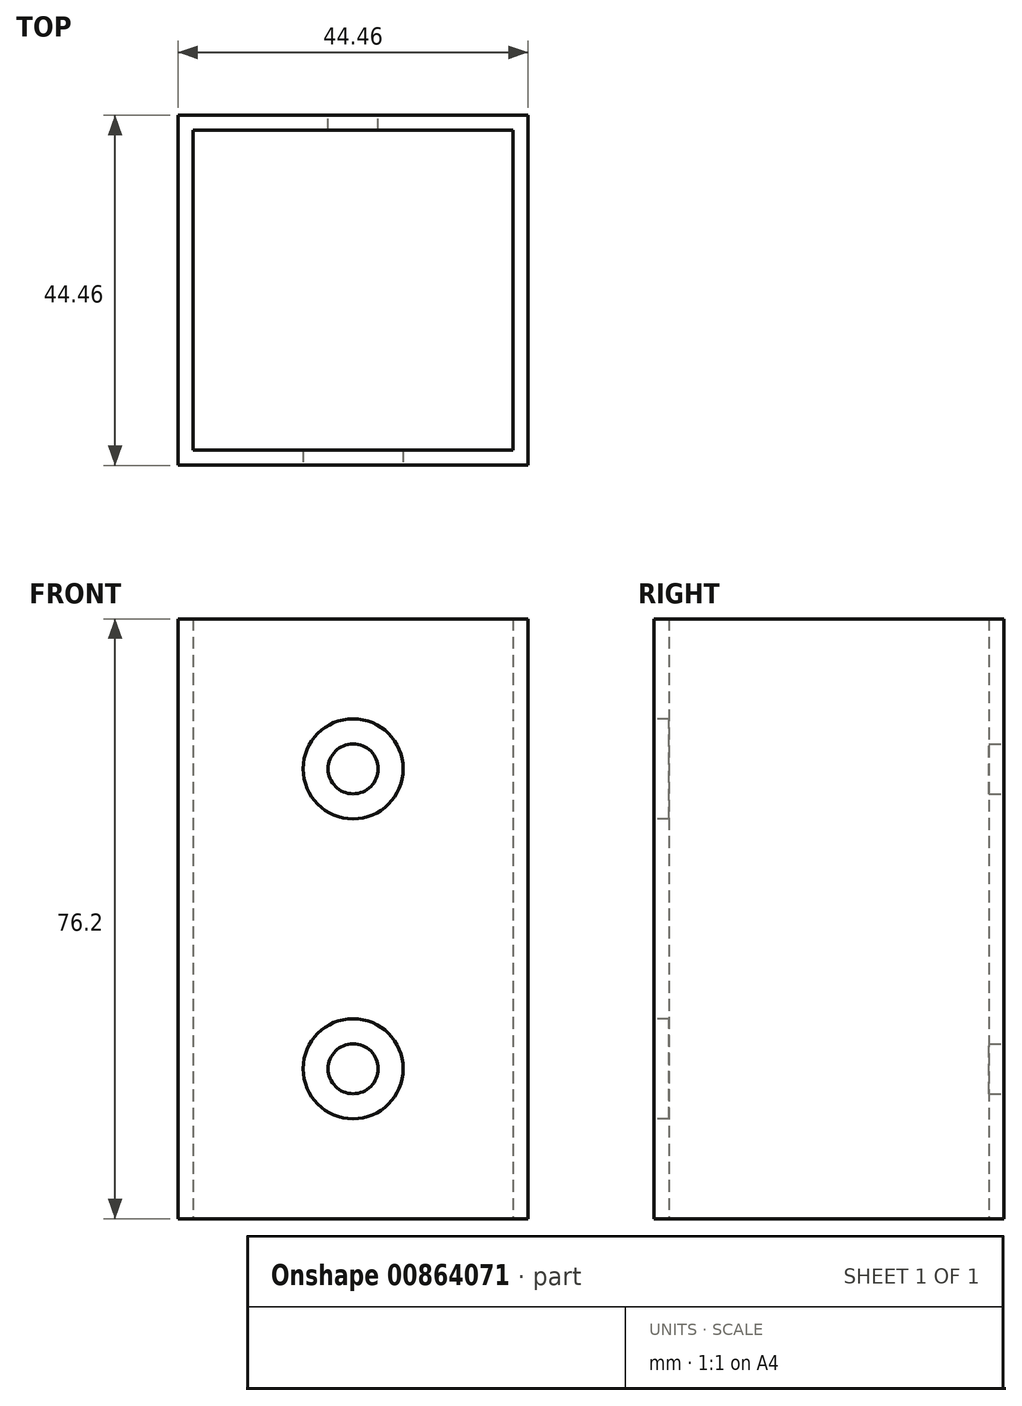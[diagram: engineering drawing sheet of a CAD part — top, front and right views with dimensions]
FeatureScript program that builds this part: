
annotation { "Feature Type Name" : "Feature", "Feature Type Description" : "" }
export const myFeature = defineFeature(function(context is Context, id is Id, definition is map)
    precondition{}
    {
        {
            var Q0;
            Q0=qCreatedBy(makeId("Top.planeOp"),FACE);
            var sketch = newSketch(context, id + "F0", { "sketchPlane" : qUnion([Q0])});
            skLineSegment(sketch, "E0.bottom", {"start": v(20.32, 20.32) * mm, "end": v(-20.32, 20.32) * mm});
            skLineSegment(sketch, "E0.top", {"start": v(20.32, -20.32) * mm, "end": v(-20.32, -20.32) * mm});
            skLineSegment(sketch, "E0.left", {"start": v(20.32, 20.32) * mm, "end": v(20.32, -20.32) * mm});
            skLineSegment(sketch, "E0.right", {"start": v(-20.32, 20.32) * mm, "end": v(-20.32, -20.32) * mm});
            skPoint(sketch, "E0.middle", {"position": v(0, 0) * mm});
            skLineSegment(sketch, "E1.bottom", {"start": v(22.23, 22.23) * mm, "end": v(-22.23, 22.22) * mm});
            skLineSegment(sketch, "E1.top", {"start": v(22.23, -22.22) * mm, "end": v(-22.23, -22.23) * mm});
            skLineSegment(sketch, "E1.left", {"start": v(22.23, 22.23) * mm, "end": v(22.23, -22.22) * mm});
            skLineSegment(sketch, "E1.right", {"start": v(-22.23, 22.22) * mm, "end": v(-22.23, -22.23) * mm});
            skSolve(sketch);
        }
        {
            var Q0;
            Q0 = qSketchRegion(id + "F0", true);
            extrude(context, id + "F1", {"entities" : qUnion([Q0]), "depth" : 76.2 * mm, "offsetDistance" : 25.4 * mm});
        }
        {
            var Q0;
            Q0=makeQuery(id+"F1.opExtrude","SWEPT_FACE",FACE,{"disambiguationData":[OSD([sQuery(id+"F0.wireOp",EDGE,"E1.top")])]});
            var sketch = newSketch(context, id + "F2", { "sketchPlane" : qUnion([Q0])});
            skCircle(sketch, "E2", {"center": v(0, 57.15) * mm, "radius": 6.35 * mm});
            skPoint(sketch, "E2.centerSnap0", {"position": v(0, 76.2) * mm});
            skCircle(sketch, "E3", {"center": v(0, 19.05) * mm, "radius": 6.35 * mm});
            skSolve(sketch);
        }
        {
            var Q0;
            Q0 = qSketchRegion(id + "F2", true);
            extrude(context, id + "F3", {"entities" : qUnion([Q0]), "operationType" : NewBodyOperationType.REMOVE, "oppositeDirection" : true, "depth" : 25.4 * mm, "offsetDistance" : 25.4 * mm});
        }
        {
            var Q0;
            Q0=makeQuery(id+"F1.opExtrude","SWEPT_FACE",FACE,{"disambiguationData":[OSD([sQuery(id+"F0.wireOp",EDGE,"E1.bottom")])]});
            var sketch = newSketch(context, id + "F4", { "sketchPlane" : qUnion([Q0])});
            skCircle(sketch, "E4", {"center": v(0, 57.15) * mm, "radius": 3.18 * mm});
            skPoint(sketch, "E4.centerSnap0", {"position": v(0, 76.2) * mm});
            skCircle(sketch, "E5", {"center": v(0, 19.05) * mm, "radius": 3.18 * mm});
            skPoint(sketch, "E5.centerSnap0", {"position": v(0, 0) * mm});
            skSolve(sketch);
        }
        {
            var Q0;
            Q0 = qSketchRegion(id + "F4", true);
            extrude(context, id + "F5", {"entities" : qUnion([Q0]), "operationType" : NewBodyOperationType.REMOVE, "oppositeDirection" : true, "depth" : 25.4 * mm, "offsetDistance" : 25.4 * mm});
        }
    });
